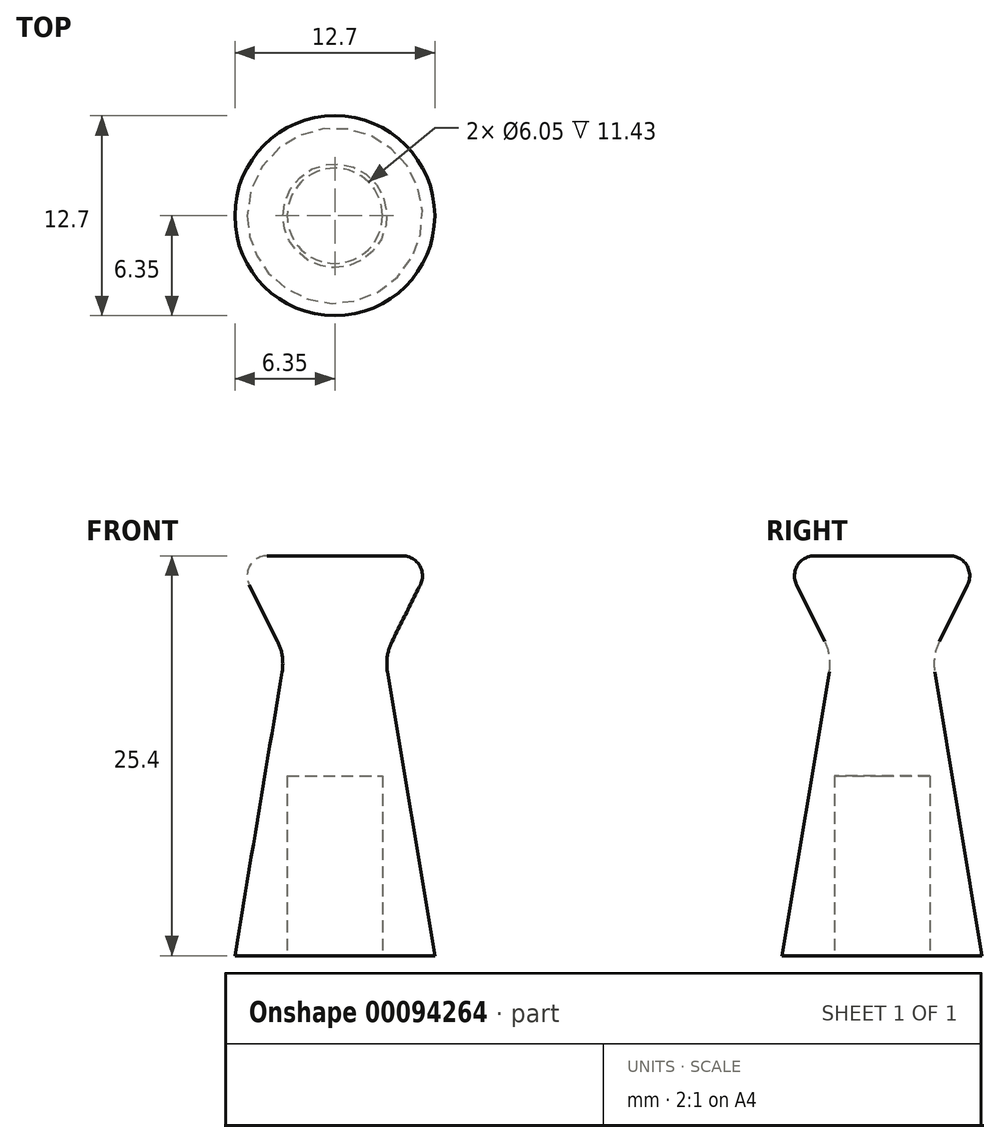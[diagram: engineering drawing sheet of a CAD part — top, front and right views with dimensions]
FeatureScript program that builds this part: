
annotation { "Feature Type Name" : "Feature", "Feature Type Description" : "" }
export const myFeature = defineFeature(function(context is Context, id is Id, definition is map)
    precondition{}
    {
        {
            var Q0;
            Q0=qCreatedBy(makeId("Front.planeOp"),FACE);
            var sketch = newSketch(context, id + "F0", { "sketchPlane" : qUnion([Q0])});
            skLineSegment(sketch, "E0", {"start": v(0, 0) * mm, "end": v(0, 25.4) * mm});
            skLineSegment(sketch, "E1", {"start": v(0, 25.4) * mm, "end": v(6.35, 25.4) * mm});
            skLineSegment(sketch, "E2", {"start": v(6.35, 25.4) * mm, "end": v(3.18, 19.05) * mm});
            skLineSegment(sketch, "E3", {"start": v(3.17, 19.05) * mm, "end": v(6.35, 0) * mm});
            skLineSegment(sketch, "E4", {"start": v(6.35, 0) * mm, "end": v(0, 0) * mm});
            skSolve(sketch);
        }
        {
            var Q0;
            Q0 = qSketchRegion(id + "F0", true);
            var Q1;
            Q1=sQuery(id+"F0.wireOp",EDGE,"E0");
            revolve(context, id + "F1", {"entities" : qUnion([Q0]), "axis" : qUnion([Q1]), "revolveType" : RevolveType.FULL});
        }
        {
            var Q0;
            Q0=makeQuery(id+"F1.opRevolve","SWEPT_FACE",FACE,{"disambiguationData":[OSD([sQuery(id+"F0.wireOp",EDGE,"E4")])]});
            var sketch = newSketch(context, id + "F2", { "sketchPlane" : qUnion([Q0])});
            skCircle(sketch, "E5", {"center": v(0, 0) * mm, "radius": 3.03 * mm});
            skSolve(sketch);
        }
        {
            var Q0;
            Q0 = qSketchRegion(id + "F2", true);
            extrude(context, id + "F3", {"entities" : qUnion([Q0]), "operationType" : NewBodyOperationType.REMOVE, "oppositeDirection" : true, "depth" : 11.43 * mm});
        }
        {
            var Q0;
            Q0=makeQuery(id+"F3.boolean.opBoolean","COPY",EDGE,{"derivedFrom":makeQuery(id+"F3.opExtrude","CAP_EDGE",EDGE,{"disambiguationData":[OSD([sQuery(id+"F2.wireOp",EDGE,"E5")])],"isStart":true})});
            var Q1;
            Q1=makeQuery(id+"F1.opRevolve","SWEPT_EDGE",EDGE,{"disambiguationData":[OSD([sQuery(id+"F0.wireOp",EDGE,"E1"),sQuery(id+"F0.wireOp",EDGE,"E2")])]});
            fillet(context, id + "F4", {"entities" : qUnion([Q0, Q1]), "radius" : 1.27 * mm, "tangentPropagation" : true, "allowEdgeOverflow" : false});
        }
        {
            var Q0;
            Q0=makeQuery(id+"F1.opRevolve","SWEPT_EDGE",EDGE,{"disambiguationData":[OSD([sQuery(id+"F0.wireOp",EDGE,"E2"),sQuery(id+"F0.wireOp",EDGE,"E3")])]});
            fillet(context, id + "F5", {"entities" : qUnion([Q0]), "radius" : 3.17 * mm, "tangentPropagation" : true, "allowEdgeOverflow" : false});
        }
        {
            var Q0;
            Q0=makeQuery(id+"F1.opRevolve","SWEPT_BODY",BODY,{"disambiguationData":[OSD([sQuery(id+"F0.wireOp",EDGE,"E0"),sQuery(id+"F0.wireOp",EDGE,"E1"),sQuery(id+"F0.wireOp",EDGE,"E2"),sQuery(id+"F0.wireOp",EDGE,"E3"),sQuery(id+"F0.wireOp",EDGE,"E4")])]});
            transform(context, id + "F6", {"entities" : qUnion([Q0]), "transformType" : TransformType.TRANSLATION_3D, "dx" : 0 * mm, "dy" : 0 * mm, "dz" : 0 * mm, "makeCopy" : true});
        }
    });
